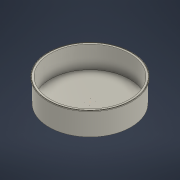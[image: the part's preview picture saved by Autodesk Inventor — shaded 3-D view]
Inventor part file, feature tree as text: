
AUTODESK INVENTOR PART (.ipt)
format: ipt  version: 2022 (Build 260153000, 153)  size: 152,064 bytes
history: native  units: mm
features: extrude x5, sketch x5, plane x2, hole x1
ambient origin geometry x8: Origin, YZ Plane, XZ Plane, XY Plane, X Axis, Y Axis, Z Axis, Center Point
bodies: Solid1 (feature_tree)
feature tree (13):
  extrude  "Extrusion1"  Depth=100.0mm TaperAngle=0.0deg
  plane  "Work Plane3"
  hole  "Hole1"  [1 undecoded]
  sketch  "Sketch6"  dims[d20=6146.6mm d21=0.0mm d22=0.0mm]
  extrude  "Extrusion5"  TaperAngle=0.0deg  [1 undecoded]
  extrude  "Extrusion6"  Depth=1600.0mm
  plane  "Work Plane4"
  extrude  "Extrusion7"  Depth=40.0mm TaperAngle=0.0deg
  extrude  "Extrusion8"  Depth=40.0mm
  sketch  "Sketch1"  dims[d1=6700.0mm d2=100.0mm d3=0.0mm]
  sketch  "Sketch5"  dims[d12=10.106mm d13=36.0mm d14=4.0mm d15=2.0mm d16=90.0deg d17=40.0mm d18=20.594885mm d19=5943.6mm]
  sketch  "Sketch7"  dims[d23=1600.0mm d24=0.0mm d25=1600.0mm]
  sketch  "Sketch8"  dims[d27=60.0mm d28=0.0mm d29=40.0mm d30=0.0mm d4=0.5mm d5=0.872665mm d6=0.5mm d7=0.872665mm]
note: 2 required parameter values undecoded (feature->parameter linkage not recoverable at this tier; creation-order binding heuristic only, values carry confidence <= 0.55)
